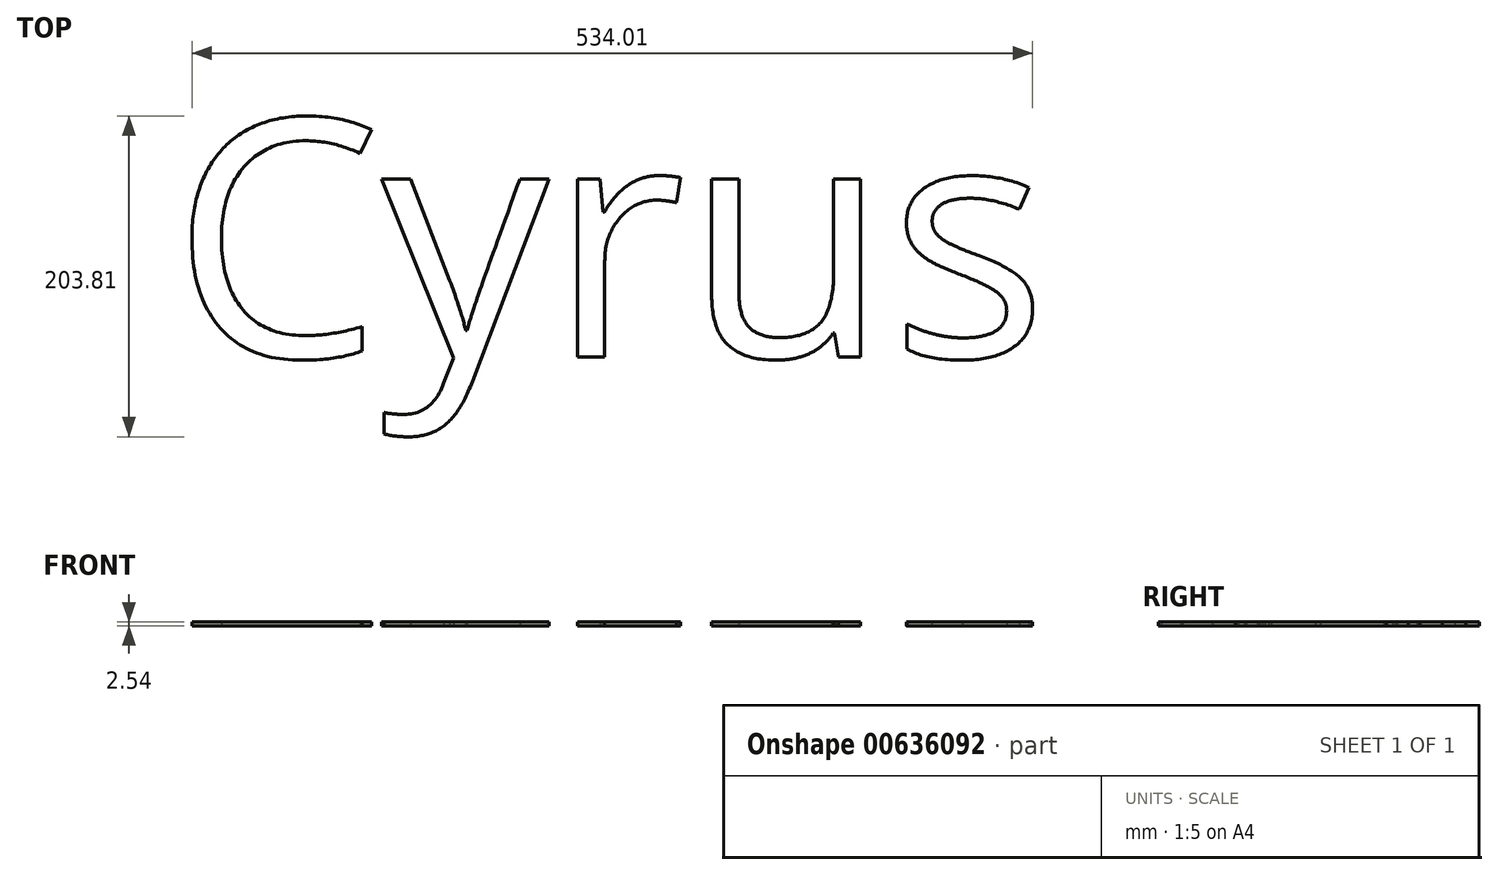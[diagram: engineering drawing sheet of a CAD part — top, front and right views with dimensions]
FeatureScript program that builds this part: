
annotation { "Feature Type Name" : "Feature", "Feature Type Description" : "" }
export const myFeature = defineFeature(function(context is Context, id is Id, definition is map)
    precondition{}
    {
        {
            var Q0;
            Q0=qCreatedBy(makeId("Top.planeOp"),FACE);
            var sketch = newSketch(context, id + "F0", { "sketchPlane" : qUnion([Q0])});
            skText(sketch, "E0", { "text": "Cyrus", "fontName": "OpenSans-Regular.ttf"});
            const initialGuessF0  = {"E0": [-0.07517, -0.0763, 1, 0, 0.15216]};
            skSetInitialGuess(sketch, initialGuessF0);
            skSolve(sketch);
        }
        {
            var Q0;
            Q0 = qSketchRegion(id + "F0", true);
            extrude(context, id + "F1", {"entities" : qUnion([Q0]), "depth" : 2.54 * mm, "offsetDistance" : 25.4 * mm});
        }
    });
